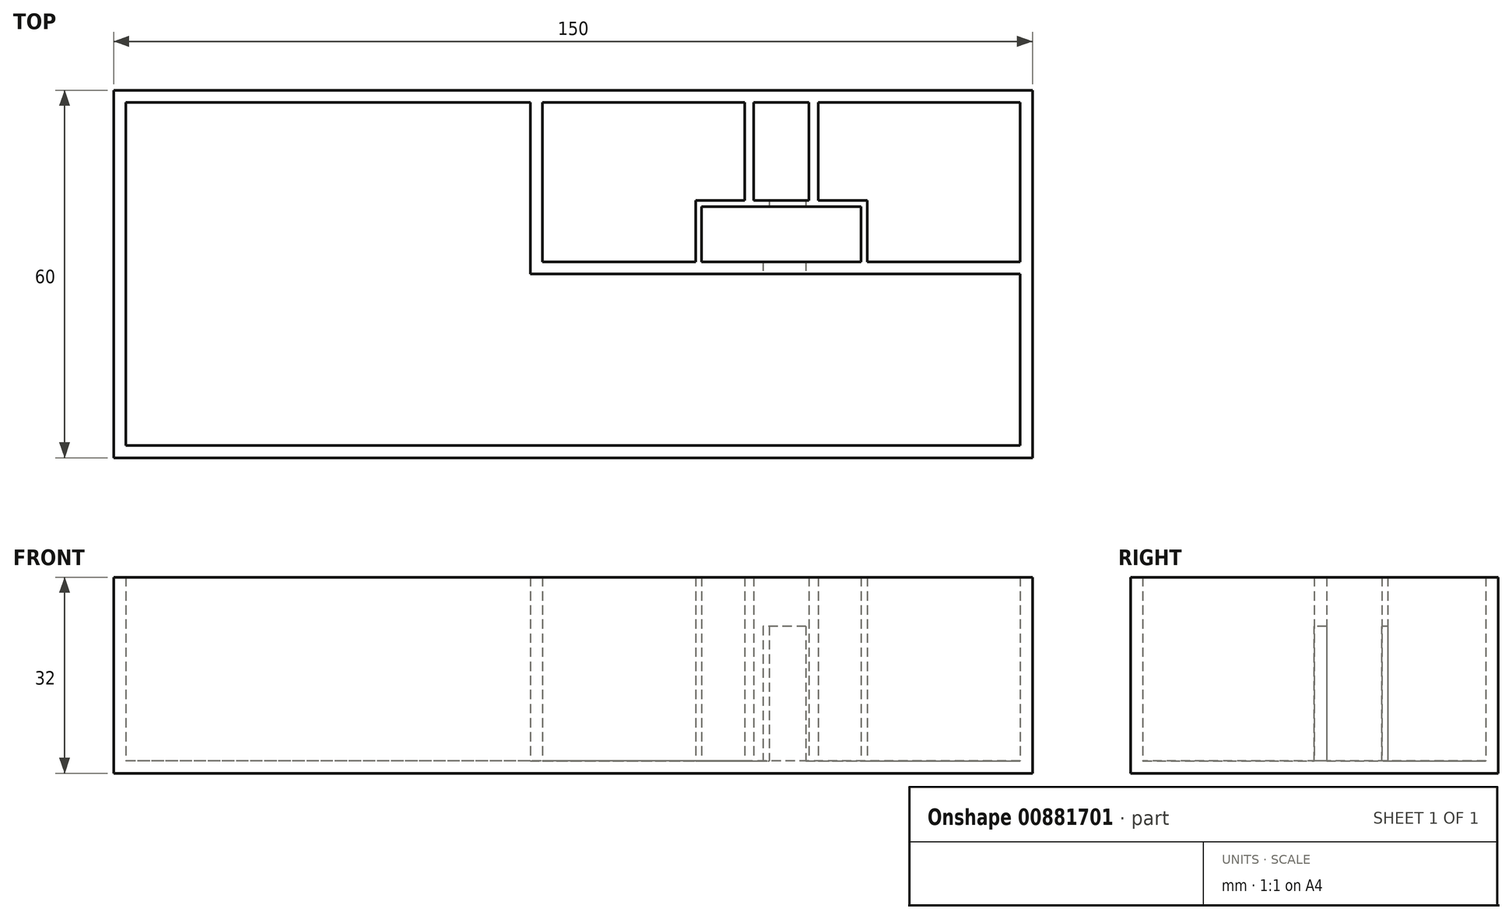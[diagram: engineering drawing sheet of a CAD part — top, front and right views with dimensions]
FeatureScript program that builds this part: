
annotation { "Feature Type Name" : "Feature", "Feature Type Description" : "" }
export const myFeature = defineFeature(function(context is Context, id is Id, definition is map)
    precondition{}
    {
        {
            var Q0;
            Q0=qCreatedBy(makeId("Top.planeOp"),FACE);
            var sketch = newSketch(context, id + "F0", { "sketchPlane" : qUnion([Q0])});
            skLineSegment(sketch, "E0.bottom", {"start": v(-57.56, -17.22) * mm, "end": v(92.44, -17.22) * mm});
            skLineSegment(sketch, "E0.top", {"start": v(-57.56, 42.78) * mm, "end": v(92.44, 42.78) * mm});
            skLineSegment(sketch, "E0.left", {"start": v(-57.56, -17.22) * mm, "end": v(-57.56, 42.78) * mm});
            skLineSegment(sketch, "E0.right", {"start": v(92.44, -17.22) * mm, "end": v(92.44, 42.78) * mm});
            skSolve(sketch);
        }
        {
            var Q0;
            Q0 = qSketchRegion(id + "F0", true);
            extrude(context, id + "F1", {"entities" : qUnion([Q0]), "depth" : 2 * mm, "offsetDistance" : 25 * mm});
        }
        {
            var Q0;
            Q0=makeQuery(id+"F1.opExtrude","CAP_FACE",FACE,{"disambiguationData":[OSD([sQuery(id+"F0.wireOp",EDGE,"E0.bottom"),sQuery(id+"F0.wireOp",EDGE,"E0.top"),sQuery(id+"F0.wireOp",EDGE,"E0.left"),sQuery(id+"F0.wireOp",EDGE,"E0.right")])],"isStart":false});
            var sketch = newSketch(context, id + "F2", { "sketchPlane" : qUnion([Q0])});
            skLineSegment(sketch, "E1.bottom", {"start": v(-57.56, 42.78) * mm, "end": v(-55.56, 42.78) * mm});
            skLineSegment(sketch, "E1.top", {"start": v(-57.56, -17.22) * mm, "end": v(-55.56, -17.22) * mm});
            skLineSegment(sketch, "E1.left", {"start": v(-57.56, 42.78) * mm, "end": v(-57.56, -17.22) * mm});
            skLineSegment(sketch, "E1.right", {"start": v(-55.56, 42.78) * mm, "end": v(-55.56, -17.22) * mm});
            skSolve(sketch);
        }
        {
            var Q0;
            Q0 = qSketchRegion(id + "F2", true);
            extrude(context, id + "F3", {"entities" : qUnion([Q0]), "operationType" : NewBodyOperationType.ADD, "depth" : 30 * mm, "offsetDistance" : 25 * mm});
        }
        {
            var Q0;
            Q0=makeQuery(id+"F1.opExtrude","CAP_FACE",FACE,{"disambiguationData":[OSD([sQuery(id+"F0.wireOp",EDGE,"E0.bottom"),sQuery(id+"F0.wireOp",EDGE,"E0.top"),sQuery(id+"F0.wireOp",EDGE,"E0.left"),sQuery(id+"F0.wireOp",EDGE,"E0.right")])],"isStart":false});
            var sketch = newSketch(context, id + "F4", { "sketchPlane" : qUnion([Q0])});
            skLineSegment(sketch, "E2.bottom", {"start": v(92.44, 42.78) * mm, "end": v(-55.56, 42.78) * mm});
            skLineSegment(sketch, "E2.top", {"start": v(92.44, 40.78) * mm, "end": v(-55.56, 40.78) * mm});
            skLineSegment(sketch, "E2.left", {"start": v(92.44, 42.78) * mm, "end": v(92.44, 40.78) * mm});
            skLineSegment(sketch, "E2.right", {"start": v(-55.56, 42.78) * mm, "end": v(-55.56, 40.78) * mm});
            skSolve(sketch);
        }
        {
            var Q0;
            Q0 = qSketchRegion(id + "F4", true);
            extrude(context, id + "F5", {"entities" : qUnion([Q0]), "operationType" : NewBodyOperationType.ADD, "depth" : 30 * mm, "offsetDistance" : 25 * mm});
        }
        {
            var Q0;
            Q0=makeQuery(id+"F1.opExtrude","CAP_FACE",FACE,{"disambiguationData":[OSD([sQuery(id+"F0.wireOp",EDGE,"E0.bottom"),sQuery(id+"F0.wireOp",EDGE,"E0.top"),sQuery(id+"F0.wireOp",EDGE,"E0.left"),sQuery(id+"F0.wireOp",EDGE,"E0.right")])],"isStart":false});
            var sketch = newSketch(context, id + "F6", { "sketchPlane" : qUnion([Q0])});
            skLineSegment(sketch, "E3.bottom", {"start": v(92.44, -17.22) * mm, "end": v(90.44, -17.22) * mm});
            skLineSegment(sketch, "E3.top", {"start": v(92.44, 40.78) * mm, "end": v(90.44, 40.78) * mm});
            skLineSegment(sketch, "E3.left", {"start": v(92.44, -17.22) * mm, "end": v(92.44, 40.78) * mm});
            skLineSegment(sketch, "E3.right", {"start": v(90.44, -17.22) * mm, "end": v(90.44, 40.78) * mm});
            skSolve(sketch);
        }
        {
            var Q0;
            Q0 = qSketchRegion(id + "F6", true);
            extrude(context, id + "F7", {"entities" : qUnion([Q0]), "operationType" : NewBodyOperationType.ADD, "depth" : 30 * mm, "offsetDistance" : 25 * mm});
        }
        {
            var Q0;
            Q0=makeQuery(id+"F1.opExtrude","CAP_FACE",FACE,{"disambiguationData":[OSD([sQuery(id+"F0.wireOp",EDGE,"E0.bottom"),sQuery(id+"F0.wireOp",EDGE,"E0.top"),sQuery(id+"F0.wireOp",EDGE,"E0.left"),sQuery(id+"F0.wireOp",EDGE,"E0.right")])],"isStart":false});
            var sketch = newSketch(context, id + "F8", { "sketchPlane" : qUnion([Q0])});
            skLineSegment(sketch, "E4.bottom", {"start": v(90.44, -17.22) * mm, "end": v(-55.56, -17.22) * mm});
            skLineSegment(sketch, "E4.top", {"start": v(90.44, -15.22) * mm, "end": v(-55.56, -15.22) * mm});
            skLineSegment(sketch, "E4.left", {"start": v(90.44, -17.22) * mm, "end": v(90.44, -15.22) * mm});
            skLineSegment(sketch, "E4.right", {"start": v(-55.56, -17.22) * mm, "end": v(-55.56, -15.22) * mm});
            skSolve(sketch);
        }
        {
            var Q0;
            Q0 = qSketchRegion(id + "F8", true);
            extrude(context, id + "F9", {"entities" : qUnion([Q0]), "operationType" : NewBodyOperationType.ADD, "depth" : 30 * mm, "offsetDistance" : 25 * mm});
        }
        {
            var Q0;
            Q0=makeQuery(id+"F1.opExtrude","CAP_FACE",FACE,{"disambiguationData":[OSD([sQuery(id+"F0.wireOp",EDGE,"E0.bottom"),sQuery(id+"F0.wireOp",EDGE,"E0.top"),sQuery(id+"F0.wireOp",EDGE,"E0.left"),sQuery(id+"F0.wireOp",EDGE,"E0.right")])],"isStart":false});
            var sketch = newSketch(context, id + "F10", { "sketchPlane" : qUnion([Q0])});
            skLineSegment(sketch, "E5.bottom", {"start": v(10.44, 40.78) * mm, "end": v(90.44, 40.78) * mm});
            skLineSegment(sketch, "E5.top", {"start": v(10.44, 12.78) * mm, "end": v(90.44, 12.78) * mm});
            skLineSegment(sketch, "E5.left", {"start": v(10.44, 40.78) * mm, "end": v(10.44, 12.78) * mm});
            skLineSegment(sketch, "E5.right", {"start": v(90.44, 40.78) * mm, "end": v(90.44, 12.78) * mm});
            skSolve(sketch);
        }
        {
            var Q0;
            Q0=makeQuery(id+"F10.imprint","IMPRINT",FACE,{"disambiguationData":[TD([[makeQuery(id+"F10.imprint","IMPRINT",EDGE,{"derivedFrom":sQuery(id+"F10.wireOp",EDGE,"E5.bottom")}),1.0]])]});
            var sketch = newSketch(context, id + "F11", { "sketchPlane" : qUnion([Q0])});
            skLineSegment(sketch, "E6.bottom", {"start": v(10.44, 12.78) * mm, "end": v(12.44, 12.78) * mm});
            skLineSegment(sketch, "E6.top", {"start": v(10.44, 40.78) * mm, "end": v(12.44, 40.78) * mm});
            skLineSegment(sketch, "E6.left", {"start": v(10.44, 12.78) * mm, "end": v(10.44, 40.78) * mm});
            skLineSegment(sketch, "E6.right", {"start": v(12.44, 12.78) * mm, "end": v(12.44, 40.78) * mm});
            skSolve(sketch);
        }
        {
            var Q0;
            Q0 = qSketchRegion(id + "F11", true);
            extrude(context, id + "F12", {"entities" : qUnion([Q0]), "operationType" : NewBodyOperationType.ADD, "depth" : 30 * mm, "offsetDistance" : 25 * mm});
        }
        {
            var Q0;
            Q0=makeQuery(id+"F10.imprint","IMPRINT",FACE,{"disambiguationData":[TD([[makeQuery(id+"F10.imprint","IMPRINT",EDGE,{"derivedFrom":sQuery(id+"F10.wireOp",EDGE,"E5.bottom")}),1.0]])]});
            var sketch = newSketch(context, id + "F13", { "sketchPlane" : qUnion([Q0])});
            skLineSegment(sketch, "E7.bottom", {"start": v(10.44, 14.78) * mm, "end": v(90.44, 14.78) * mm});
            skLineSegment(sketch, "E7.top", {"start": v(10.44, 12.78) * mm, "end": v(90.44, 12.78) * mm});
            skLineSegment(sketch, "E7.left", {"start": v(10.44, 14.78) * mm, "end": v(10.44, 12.78) * mm});
            skLineSegment(sketch, "E7.right", {"start": v(90.44, 14.78) * mm, "end": v(90.44, 12.78) * mm});
            skSolve(sketch);
        }
        {
            var Q0;
            Q0 = qSketchRegion(id + "F13", true);
            extrude(context, id + "F14", {"entities" : qUnion([Q0]), "operationType" : NewBodyOperationType.ADD, "depth" : 30 * mm, "offsetDistance" : 25 * mm});
        }
        {
            var Q0;
            Q0=makeQuery(id+"F10.imprint","IMPRINT",FACE,{"disambiguationData":[TD([[makeQuery(id+"F10.imprint","IMPRINT",EDGE,{"derivedFrom":sQuery(id+"F10.wireOp",EDGE,"E5.bottom")}),1.0]])]});
            var sketch = newSketch(context, id + "F15", { "sketchPlane" : qUnion([Q0])});
            skLineSegment(sketch, "E8.bottom", {"start": v(37.44, 14.78) * mm, "end": v(65.44, 14.78) * mm});
            skLineSegment(sketch, "E8.top", {"start": v(37.44, 24.78) * mm, "end": v(65.44, 24.78) * mm});
            skLineSegment(sketch, "E8.left", {"start": v(37.44, 14.78) * mm, "end": v(37.44, 24.78) * mm});
            skLineSegment(sketch, "E8.right", {"start": v(65.44, 14.78) * mm, "end": v(65.44, 24.78) * mm});
            skSolve(sketch);
        }
        {
            var Q0;
            Q0=makeQuery(id+"F15.imprint","IMPRINT",FACE,{"disambiguationData":[TD([[makeQuery(id+"F15.imprint","IMPRINT",EDGE,{"derivedFrom":sQuery(id+"F15.wireOp",EDGE,"E8.bottom")}),1.0]])]});
            var sketch = newSketch(context, id + "F16", { "sketchPlane" : qUnion([Q0])});
            skLineSegment(sketch, "E9.bottom", {"start": v(37.44, 14.78) * mm, "end": v(38.44, 14.78) * mm});
            skLineSegment(sketch, "E9.top", {"start": v(37.44, 24.78) * mm, "end": v(38.44, 24.78) * mm});
            skLineSegment(sketch, "E9.left", {"start": v(37.44, 14.78) * mm, "end": v(37.44, 24.78) * mm});
            skLineSegment(sketch, "E9.right", {"start": v(38.44, 14.78) * mm, "end": v(38.44, 24.78) * mm});
            skSolve(sketch);
        }
        {
            var Q0;
            Q0 = qSketchRegion(id + "F16", true);
            extrude(context, id + "F17", {"entities" : qUnion([Q0]), "operationType" : NewBodyOperationType.ADD, "depth" : 30 * mm, "offsetDistance" : 25 * mm});
        }
        {
            var Q0;
            Q0=makeQuery(id+"F15.imprint","IMPRINT",FACE,{"disambiguationData":[TD([[makeQuery(id+"F15.imprint","IMPRINT",EDGE,{"derivedFrom":sQuery(id+"F15.wireOp",EDGE,"E8.bottom")}),1.0]])]});
            var sketch = newSketch(context, id + "F18", { "sketchPlane" : qUnion([Q0])});
            skLineSegment(sketch, "E10.bottom", {"start": v(37.44, 23.78) * mm, "end": v(65.44, 23.78) * mm});
            skLineSegment(sketch, "E10.top", {"start": v(37.44, 24.78) * mm, "end": v(65.44, 24.78) * mm});
            skLineSegment(sketch, "E10.left", {"start": v(37.44, 23.78) * mm, "end": v(37.44, 24.78) * mm});
            skLineSegment(sketch, "E10.right", {"start": v(65.44, 23.78) * mm, "end": v(65.44, 24.78) * mm});
            skSolve(sketch);
        }
        {
            var Q0;
            Q0 = qSketchRegion(id + "F18", true);
            extrude(context, id + "F19", {"entities" : qUnion([Q0]), "operationType" : NewBodyOperationType.ADD, "depth" : 30 * mm, "offsetDistance" : 25 * mm});
        }
        {
            var Q0;
            Q0=makeQuery(id+"F15.imprint","IMPRINT",FACE,{"disambiguationData":[TD([[makeQuery(id+"F15.imprint","IMPRINT",EDGE,{"derivedFrom":sQuery(id+"F15.wireOp",EDGE,"E8.bottom")}),1.0]])]});
            var sketch = newSketch(context, id + "F20", { "sketchPlane" : qUnion([Q0])});
            skLineSegment(sketch, "E11.bottom", {"start": v(64.44, 14.78) * mm, "end": v(65.44, 14.78) * mm});
            skLineSegment(sketch, "E11.top", {"start": v(64.44, 24.78) * mm, "end": v(65.44, 24.78) * mm});
            skLineSegment(sketch, "E11.left", {"start": v(64.44, 14.78) * mm, "end": v(64.44, 24.78) * mm});
            skLineSegment(sketch, "E11.right", {"start": v(65.44, 14.78) * mm, "end": v(65.44, 24.78) * mm});
            skSolve(sketch);
        }
        {
            var Q0;
            Q0 = qSketchRegion(id + "F20", true);
            extrude(context, id + "F21", {"entities" : qUnion([Q0]), "operationType" : NewBodyOperationType.ADD, "depth" : 30 * mm, "offsetDistance" : 25 * mm});
        }
        {
            var Q0;
            Q0=makeQuery(id+"F10.imprint","IMPRINT",FACE,{"disambiguationData":[TD([[makeQuery(id+"F10.imprint","IMPRINT",EDGE,{"derivedFrom":sQuery(id+"F10.wireOp",EDGE,"E5.bottom")}),1.0]])]});
            var sketch = newSketch(context, id + "F22", { "sketchPlane" : qUnion([Q0])});
            skLineSegment(sketch, "E12.bottom", {"start": v(45.44, 40.78) * mm, "end": v(46.94, 40.78) * mm});
            skLineSegment(sketch, "E12.top", {"start": v(45.44, 24.78) * mm, "end": v(46.94, 24.78) * mm});
            skLineSegment(sketch, "E12.left", {"start": v(45.44, 40.78) * mm, "end": v(45.44, 24.78) * mm});
            skLineSegment(sketch, "E12.right", {"start": v(46.94, 40.78) * mm, "end": v(46.94, 24.78) * mm});
            skSolve(sketch);
        }
        {
            var Q0;
            Q0 = qSketchRegion(id + "F22", true);
            extrude(context, id + "F23", {"entities" : qUnion([Q0]), "operationType" : NewBodyOperationType.ADD, "depth" : 30 * mm, "offsetDistance" : 25 * mm});
        }
        {
            var Q0;
            Q0=makeQuery(id+"F10.imprint","IMPRINT",FACE,{"disambiguationData":[TD([[makeQuery(id+"F10.imprint","IMPRINT",EDGE,{"derivedFrom":sQuery(id+"F10.wireOp",EDGE,"E5.bottom")}),1.0]])]});
            var sketch = newSketch(context, id + "F24", { "sketchPlane" : qUnion([Q0])});
            skLineSegment(sketch, "E13.bottom", {"start": v(55.94, 24.78) * mm, "end": v(57.44, 24.78) * mm});
            skLineSegment(sketch, "E13.top", {"start": v(55.94, 40.78) * mm, "end": v(57.44, 40.78) * mm});
            skLineSegment(sketch, "E13.left", {"start": v(55.94, 24.78) * mm, "end": v(55.94, 40.78) * mm});
            skLineSegment(sketch, "E13.right", {"start": v(57.44, 24.78) * mm, "end": v(57.44, 40.78) * mm});
            skSolve(sketch);
        }
        {
            var Q0;
            Q0 = qSketchRegion(id + "F24", true);
            extrude(context, id + "F25", {"entities" : qUnion([Q0]), "operationType" : NewBodyOperationType.ADD, "depth" : 30 * mm, "offsetDistance" : 25 * mm});
        }
        {
            var Q0;
            Q0=makeQuery(id+"F14.boolean.opBoolean","MERGE",FACE,{"derivedFrom":[makeQuery(id+"F12.opExtrude","SWEPT_FACE",FACE,{"disambiguationData":[OSD([sQuery(id+"F11.wireOp",EDGE,"E6.bottom")])]}),makeQuery(id+"F14.opExtrude","SWEPT_FACE",FACE,{"disambiguationData":[OSD([sQuery(id+"F13.wireOp",EDGE,"E7.top")])]})]});
            var sketch = newSketch(context, id + "F26", { "sketchPlane" : qUnion([Q0])});
            skLineSegment(sketch, "E14.bottom", {"start": v(48.44, 2) * mm, "end": v(55.44, 2) * mm});
            skLineSegment(sketch, "E14.top", {"start": v(48.44, 24) * mm, "end": v(55.44, 24) * mm});
            skLineSegment(sketch, "E14.left", {"start": v(48.44, 2) * mm, "end": v(48.44, 24) * mm});
            skLineSegment(sketch, "E14.right", {"start": v(55.44, 2) * mm, "end": v(55.44, 24) * mm});
            skSolve(sketch);
        }
        {
            var Q0;
            Q0 = qSketchRegion(id + "F26", true);
            extrude(context, id + "F27", {"entities" : qUnion([Q0]), "operationType" : NewBodyOperationType.REMOVE, "oppositeDirection" : true, "depth" : 3 * mm, "offsetDistance" : 25 * mm});
        }
        {
            var Q0;
            Q0=makeQuery(id+"F19.opExtrude","SWEPT_FACE",FACE,{"disambiguationData":[OSD([sQuery(id+"F18.wireOp",EDGE,"E10.bottom")])]});
            var sketch = newSketch(context, id + "F28", { "sketchPlane" : qUnion([Q0])});
            skLineSegment(sketch, "E15.bottom", {"start": v(49.44, 2) * mm, "end": v(55.44, 2) * mm});
            skLineSegment(sketch, "E15.top", {"start": v(49.44, 24) * mm, "end": v(55.44, 24) * mm});
            skLineSegment(sketch, "E15.left", {"start": v(49.44, 2) * mm, "end": v(49.44, 24) * mm});
            skLineSegment(sketch, "E15.right", {"start": v(55.44, 2) * mm, "end": v(55.44, 24) * mm});
            skSolve(sketch);
        }
        {
            var Q0;
            Q0 = qSketchRegion(id + "F28", true);
            extrude(context, id + "F29", {"entities" : qUnion([Q0]), "operationType" : NewBodyOperationType.REMOVE, "oppositeDirection" : true, "depth" : 2 * mm, "offsetDistance" : 25 * mm});
        }
    });
